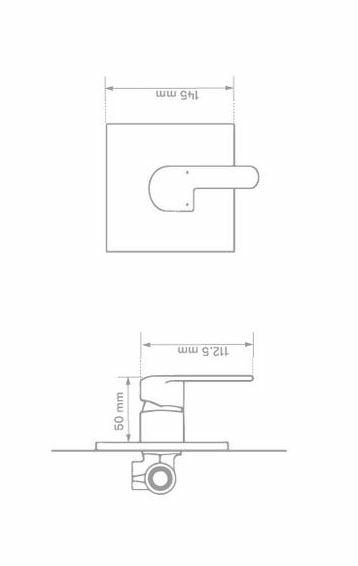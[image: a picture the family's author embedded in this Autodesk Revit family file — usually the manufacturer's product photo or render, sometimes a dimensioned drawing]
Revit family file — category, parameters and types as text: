
# Revit family: 01-1802-11-MEZCLADOR LAVAMANOS PLÁSTICO TEDESCA
name_source: partatom
category: Plumbing Fixtures
revit_build: Autodesk Revit 2018 (Build: 20170223_1515(x64)
units: mm (PartAtom-declared; Revit-internal decimal feet)

## family parameters
Cut with Voids When Loaded = No
Host = Face
OmniClass Number = 23.31.11.00
Part Type = Normal
Room Calculation Point = No
Round Connector Dimension = Use Diameter
Shared = No

## types (1)
- 01-1802-11
    Alto = 87 mm
    Ancho = 218 mm
    CW Connection = Yes
    Default Elevation = 0 mm  [stored 0 ft]
    Description = Griferia bimando baño
    HW Connection = Yes
    Largo = 129 mm
    Link Ficha Tecnica = http://infotecnica.gricol.com
    Manufacturer = Gricol
    Model = 01-1802-11
    Plastico ABS Cromado = Plastico ABS Cromado
    Product Name = MEZCLADOR LAVAMANOS PLÁSTICO COLECCIÓN TEDESCA
    Type Image = MEZCLADOR LAVAMANOS TEDESCA FOTO.JPG
    URL = https://www.gricol.com
    Vent Connection = No
    Waste Connection = No

note: [stored X ft] marks values corroborated as IEEE doubles in the binary element streams (Revit-internal decimal feet)

## geometry (parser evidence)
native form markers: Blend x2, Sweep x6
no freeform markers — native parametric forms only
